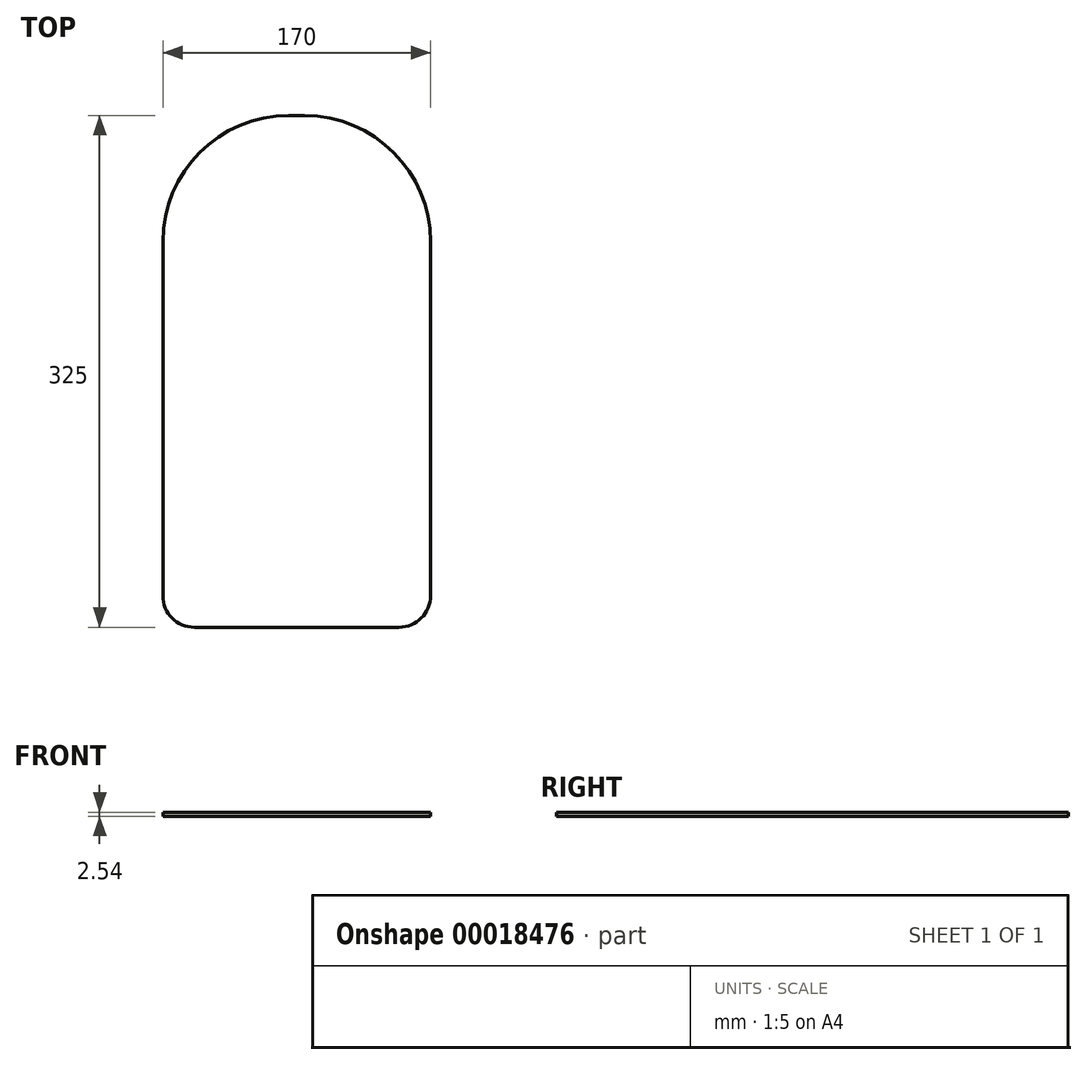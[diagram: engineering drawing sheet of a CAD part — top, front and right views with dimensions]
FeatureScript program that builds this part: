
annotation { "Feature Type Name" : "Feature", "Feature Type Description" : "" }
export const myFeature = defineFeature(function(context is Context, id is Id, definition is map)
    precondition{}
    {
        {
            var Q0;
            Q0=qCreatedBy(makeId("Top.planeOp"),FACE);
            var sketch = newSketch(context, id + "F0", { "sketchPlane" : qUnion([Q0])});
            skLineSegment(sketch, "E0.rect.bottom", {"start": v(65, -162.5) * mm, "end": v(-65, -162.5) * mm});
            skLineSegment(sketch, "E0.rect.top", {"start": v(5, 162.5) * mm, "end": v(-5, 162.5) * mm});
            skLineSegment(sketch, "E0.rect.left", {"start": v(85, -142.5) * mm, "end": v(85, 82.5) * mm});
            skLineSegment(sketch, "E0.rect.right", {"start": v(-85, -142.5) * mm, "end": v(-85, 82.5) * mm});
            skPoint(sketch, "E0.rect.middle", {"position": v(0, 0) * mm});
            skPoint(sketch, "E1.visualSharp", {"position": v(85, -162.5) * mm});
            skArc(sketch, "E1.filletArc", {"start": v(65, -162.5) * mm, "mid": v(79.14, -156.64) * mm, "end": v(85, -142.5) * mm});
            skPoint(sketch, "E2.visualSharp", {"position": v(-85, -162.5) * mm});
            skArc(sketch, "E2.filletArc", {"start": v(-85, -142.5) * mm, "mid": v(-79.14, -156.64) * mm, "end": v(-65, -162.5) * mm});
            skPoint(sketch, "E3.visualSharp", {"position": v(-85, 162.5) * mm});
            skArc(sketch, "E3.filletArc", {"start": v(-5, 162.5) * mm, "mid": v(-61.57, 139.07) * mm, "end": v(-85, 82.5) * mm});
            skPoint(sketch, "E4.visualSharp", {"position": v(85, 162.5) * mm});
            skArc(sketch, "E4.filletArc", {"start": v(85, 82.5) * mm, "mid": v(61.57, 139.07) * mm, "end": v(5, 162.5) * mm});
            skSolve(sketch);
        }
        {
            var Q0;
            Q0=qSketchRegion(id+"F0",true);
            extrude(context, id + "F1", {"entities" : qUnion([Q0]), "depth" : 2.54 * mm});
        }
    });
